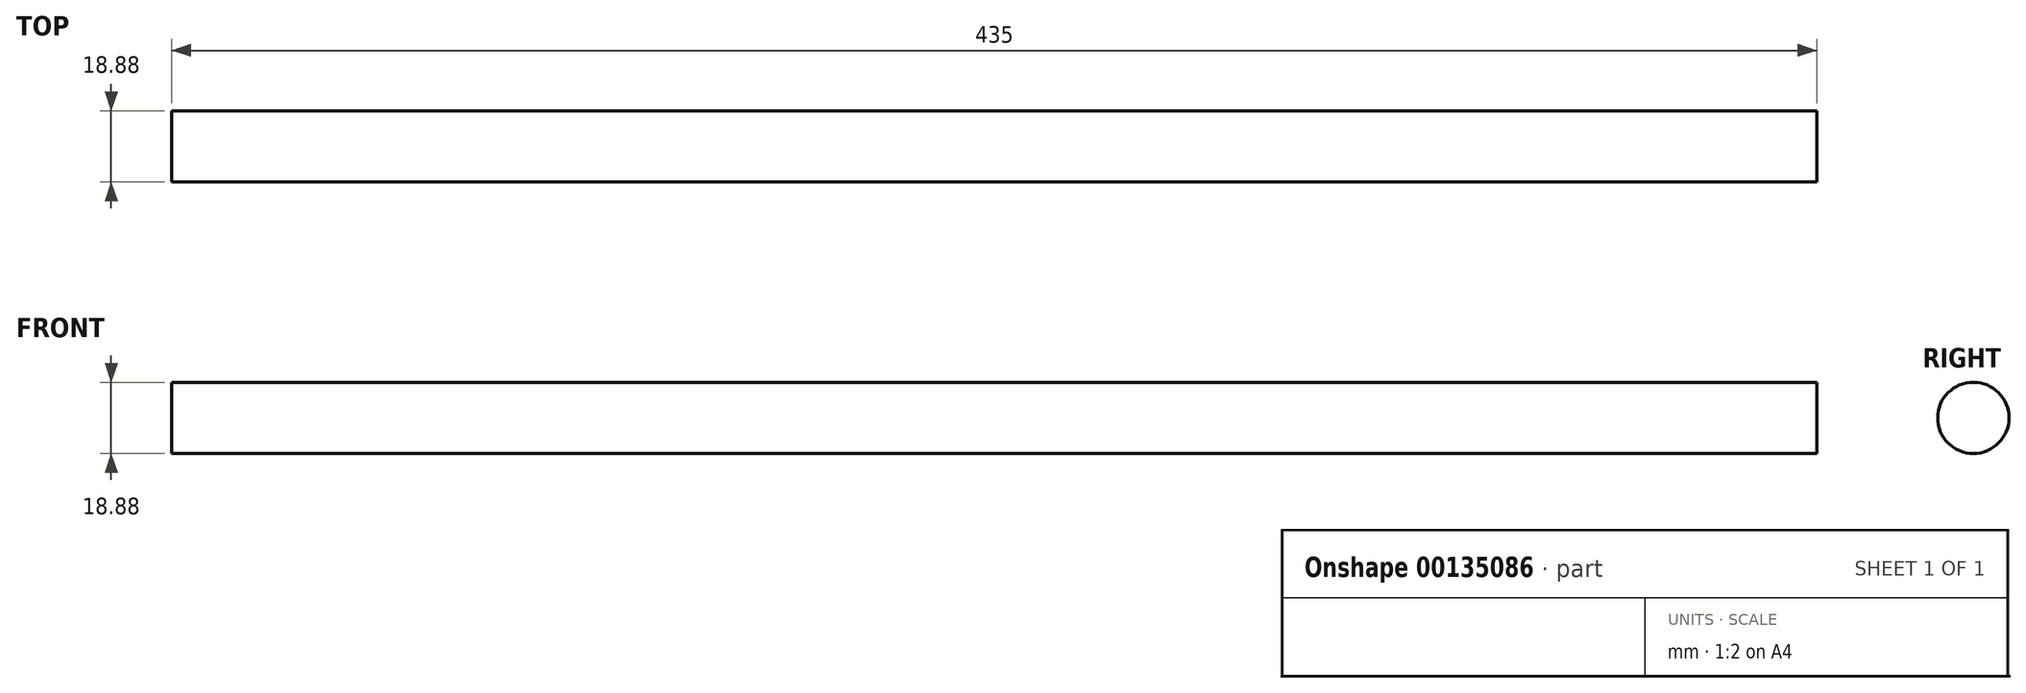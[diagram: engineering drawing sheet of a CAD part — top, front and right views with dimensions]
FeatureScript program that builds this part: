
annotation { "Feature Type Name" : "Feature", "Feature Type Description" : "" }
export const myFeature = defineFeature(function(context is Context, id is Id, definition is map)
    precondition{}
    {
        {
            var Q0;
            Q0=qCreatedBy(makeId("Right.planeOp"),FACE);
            var sketch = newSketch(context, id + "F0", { "sketchPlane" : qUnion([Q0])});
            skCircle(sketch, "E0", {"center": v(0, 0) * mm, "radius": 9.44 * mm});
            skSolve(sketch);
        }
        {
            var Q0;
            Q0=makeQuery(id+"F0.imprint","IMPRINT",FACE,{"disambiguationData":[TD([[makeQuery(id+"F0.imprint","IMPRINT",EDGE,{"derivedFrom":sQuery(id+"F0.wireOp",EDGE,"E0")}),1.0]])]});
            extrude(context, id + "F1", {"entities" : qUnion([Q0]), "endBound" : BoundingType.SYMMETRIC, "depth" : 435 * mm});
        }
    });
